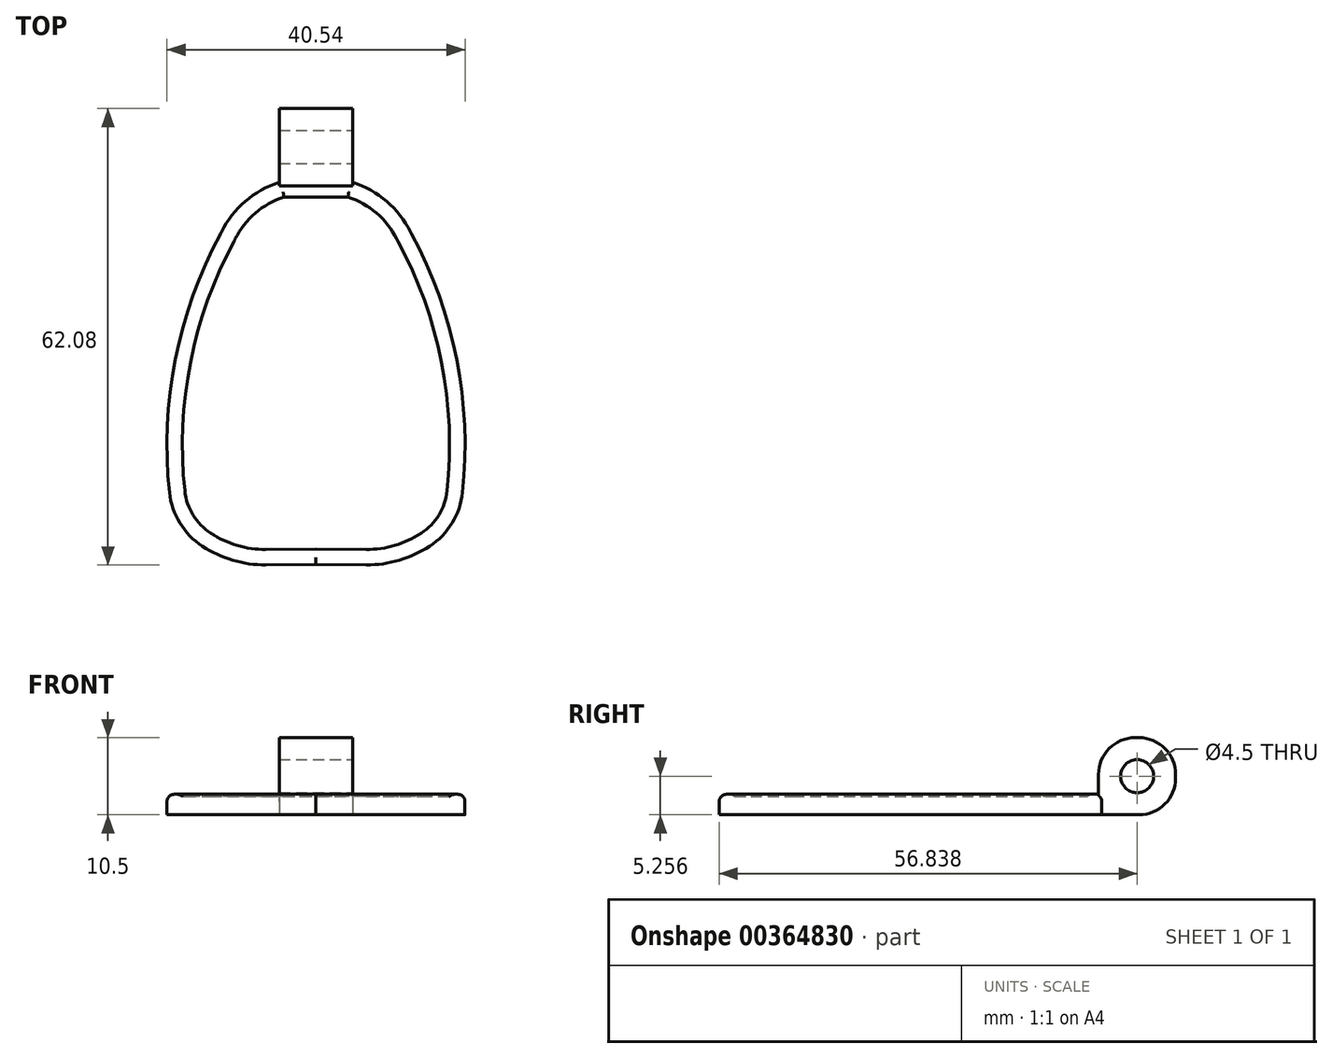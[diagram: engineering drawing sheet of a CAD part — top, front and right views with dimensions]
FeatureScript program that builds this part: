
annotation { "Feature Type Name" : "Feature", "Feature Type Description" : "" }
export const myFeature = defineFeature(function(context is Context, id is Id, definition is map)
    precondition{}
    {
        {
            var Q0;
            Q0=qCreatedBy(makeId("Top.planeOp"),FACE);
            var sketch = newSketch(context, id + "F0", { "sketchPlane" : qUnion([Q0])});
            skPoint(sketch, "E0.endSnap0", {"position": v(-0.73, -44.7) * mm});
            skArc(sketch, "E1", {"start": v(12.92, 6.57) * mm, "mid": v(8.04, 12.02) * mm, "end": v(1.01, 14.08) * mm});
            skArc(sketch, "E2", {"start": v(19.44, -32.3) * mm, "mid": v(19.43, -12.32) * mm, "end": v(12.92, 6.57) * mm});
            skArc(sketch, "E3.0", {"start": v(11.05, 5.6) * mm, "mid": v(6.94, 10.23) * mm, "end": v(1, 11.98) * mm});
            skArc(sketch, "E3.1", {"start": v(17.44, -31.52) * mm, "mid": v(17.32, -12.43) * mm, "end": v(11.05, 5.6) * mm});
            skArc(sketch, "E3.2", {"start": v(9.45, -35.83) * mm, "mid": v(13.96, -34.64) * mm, "end": v(17.44, -31.52) * mm});
            skArc(sketch, "E3.3", {"start": v(0, -36.35) * mm, "mid": v(4.75, -36.53) * mm, "end": v(9.45, -35.83) * mm});
            skPoint(sketch, "E4.orphan", {"position": v(0, 29.56) * mm});
            skPoint(sketch, "E0.end.orphan", {"position": v(-0.73, -55.53) * mm});
            skPoint(sketch, "E5.start.orphan", {"position": v(-6.8, -38.6) * mm});
            skPoint(sketch, "E6.visualSharp", {"position": v(-18.12, -32.94) * mm});
            skLineSegment(sketch, "E7", {"start": v(0, 11.88) * mm, "end": v(0, -48) * mm});
            skArc(sketch, "E8.MirrorCS", {"start": v(-11.05, 5.6) * mm, "mid": v(-6.94, 10.23) * mm, "end": v(-1, 11.98) * mm});
            skArc(sketch, "E9.MirrorCS", {"start": v(-17.44, -31.52) * mm, "mid": v(-17.32, -12.43) * mm, "end": v(-11.05, 5.6) * mm});
            skArc(sketch, "E10.MirrorCS", {"start": v(-9.45, -35.83) * mm, "mid": v(-13.96, -34.64) * mm, "end": v(-17.44, -31.52) * mm});
            skArc(sketch, "E11.MirrorCS", {"start": v(0, -36.35) * mm, "mid": v(-4.75, -36.53) * mm, "end": v(-9.45, -35.83) * mm});
            skArc(sketch, "E12.MirrorCS", {"start": v(-19.44, -32.3) * mm, "mid": v(-19.43, -12.32) * mm, "end": v(-12.92, 6.57) * mm});
            skArc(sketch, "E13.MirrorCS", {"start": v(-12.92, 6.57) * mm, "mid": v(-8.04, 12.02) * mm, "end": v(-1.01, 14.08) * mm});
            skLineSegment(sketch, "E14.bottom", {"start": v(5, 12.98) * mm, "end": v(-5, 12.98) * mm});
            skLineSegment(sketch, "E14.top", {"start": v(5, 23.48) * mm, "end": v(-5, 23.48) * mm});
            skLineSegment(sketch, "E14.left", {"start": v(5, 12.98) * mm, "end": v(5, 23.48) * mm});
            skLineSegment(sketch, "E14.right", {"start": v(-5, 12.98) * mm, "end": v(-5, 23.48) * mm});
            skPoint(sketch, "E14.middle", {"position": v(0, 18.23) * mm});
            skLineSegment(sketch, "E15", {"start": v(-1, 11.98) * mm, "end": v(1, 11.98) * mm});
            skPoint(sketch, "E16.MirrorCS.end.orphan", {"position": v(-9.73, -37.92) * mm});
            skPoint(sketch, "E17.MirrorCS.end.orphan", {"position": v(-19.44, -32.3) * mm});
            skPoint(sketch, "E18.orphan", {"position": v(-1.4, -38.6) * mm});
            skPoint(sketch, "E19.start.orphan", {"position": v(1.4, -38.6) * mm});
            skPoint(sketch, "E20.start.orphan", {"position": v(9.73, -37.92) * mm});
            skArc(sketch, "E21", {"start": v(-19.44, -32.3) * mm, "mid": v(-13.87, -36.96) * mm, "end": v(-6.8, -38.6) * mm});
            skLineSegment(sketch, "E22", {"start": v(-6.8, -38.6) * mm, "end": v(0, -38.56) * mm});
            skLineSegment(sketch, "E23.MirrorCS", {"start": v(6.8, -38.6) * mm, "end": v(0, -38.56) * mm});
            skArc(sketch, "E24.MirrorCS", {"start": v(19.44, -32.3) * mm, "mid": v(13.87, -36.96) * mm, "end": v(6.8, -38.6) * mm});
            skSolve(sketch);
        }
        {
            var Q0;
            {var subQ3=sQuery(id+"F0.wireOp",EDGE,"E14.bottom");Q0=makeQuery(id+"F0.imprint","IMPRINT",FACE,{"disambiguationData":[TD([[makeQuery(id+"F0.imprint","IMPRINT",EDGE,{"derivedFrom":subQ3}),-1.0]])]});}
            var Q1;
            Q1=makeQuery(id+"F0.imprint","IMPRINT",FACE,{"disambiguationData":[TD([[makeQuery(id+"F0.imprint","IMPRINT",EDGE,{"derivedFrom":sQuery(id+"F0.wireOp",EDGE,"E3.0")}),1.0]])]});
            var Q2;
            {var subQ0=sQuery(id+"F0.wireOp",EDGE,"E2");Q2=makeQuery(id+"F0.imprint","IMPRINT",FACE,{"disambiguationData":[TD([[makeQuery(id+"F0.imprint","IMPRINT",EDGE,{"derivedFrom":subQ0}),1.0]])]});}
            extrude(context, id + "F1", {"entities" : qUnion([Q0, Q1, Q2]), "depth" : 2.5 * mm});
        }
        {
            var Q0;
            {var subQ3=sQuery(id+"F0.wireOp",EDGE,"E14.bottom");Q0=makeQuery(id+"F0.imprint","IMPRINT",FACE,{"disambiguationData":[TD([[makeQuery(id+"F0.imprint","IMPRINT",EDGE,{"derivedFrom":subQ3}),-1.0]])]});}
            extrude(context, id + "F2", {"entities" : qUnion([Q0]), "operationType" : NewBodyOperationType.ADD, "depth" : 10.5 * mm});
        }
        {
            var Q0;
            Q0=makeQuery(id+"F2.opExtrude","CAP_EDGE",EDGE,{"disambiguationData":[OSD([sQuery(id+"F0.wireOp",EDGE,"E14.top")])],"isStart":false});
            var Q1;
            Q1=makeQuery(id+"F2.opExtrude","CAP_EDGE",EDGE,{"disambiguationData":[OSD([sQuery(id+"F0.wireOp",EDGE,"E14.bottom")])],"isStart":false});
            var Q2;
            Q2=makeQuery(id+"F1.opExtrude","CAP_EDGE",EDGE,{"disambiguationData":[OSD([sQuery(id+"F0.wireOp",EDGE,"E14.top")])],"isStart":true});
            fillet(context, id + "F3", {"entities" : qUnion([Q0, Q1, Q2]), "radius" : 5 * mm, "tangentPropagation" : true, "allowEdgeOverflow" : false});
        }
        {
            var Q0;
            Q0=makeQuery(id+"F1.opExtrude","SWEPT_EDGE",EDGE,{"disambiguationData":[OSD([sQuery(id+"F0.wireOp",EDGE,"E2"),sQuery(id+"F0.wireOp",EDGE,"E20")])]});
            var Q1;
            Q1=makeQuery(id+"F1.opExtrude","SWEPT_EDGE",EDGE,{"disambiguationData":[OSD([sQuery(id+"F0.wireOp",EDGE,"E1"),sQuery(id+"F0.wireOp",EDGE,"E2")])]});
            var Q2;
            Q2=makeQuery(id+"F1.opExtrude","SWEPT_EDGE",EDGE,{"disambiguationData":[OSD([sQuery(id+"F0.wireOp",EDGE,"E12.MirrorCS"),sQuery(id+"F0.wireOp",EDGE,"E13.MirrorCS")])]});
            var Q3;
            Q3=makeQuery(id+"F1.opExtrude","SWEPT_EDGE",EDGE,{"disambiguationData":[OSD([sQuery(id+"F0.wireOp",EDGE,"E17.MirrorCS"),sQuery(id+"F0.wireOp",EDGE,"E12.MirrorCS")])]});
            fillet(context, id + "F4", {"entities" : qUnion([Q0, Q1, Q2, Q3]), "radius" : 10 * mm, "tangentPropagation" : true, "allowEdgeOverflow" : false});
        }
        {
            var Q0;
            Q0=makeQuery(id+"F1.opExtrude","CAP_FACE",FACE,{"disambiguationData":[OSD([sQuery(id+"F0.wireOp",EDGE,"E1"),sQuery(id+"F0.wireOp",EDGE,"E2"),sQuery(id+"F0.wireOp",EDGE,"E12.MirrorCS"),sQuery(id+"F0.wireOp",EDGE,"E13.MirrorCS"),sQuery(id+"F0.wireOp",EDGE,"E14.top"),sQuery(id+"F0.wireOp",EDGE,"E14.left"),sQuery(id+"F0.wireOp",EDGE,"E14.right"),sQuery(id+"F0.wireOp",EDGE,"E21"),sQuery(id+"F0.wireOp",EDGE,"E22"),sQuery(id+"F0.wireOp",EDGE,"E23.MirrorCS"),sQuery(id+"F0.wireOp",EDGE,"E24.MirrorCS")])],"isStart":false});
            var sketch = newSketch(context, id + "F5", { "sketchPlane" : qUnion([Q0])});
            skArc(sketch, "E25.0", {"start": v(10.98, 5.76) * mm, "mid": v(8.24, 9.27) * mm, "end": v(4.36, 11.44) * mm});
            skArc(sketch, "E25.1", {"start": v(11.16, 5.41) * mm, "mid": v(11.06, 5.58) * mm, "end": v(10.98, 5.76) * mm});
            skArc(sketch, "E25.2", {"start": v(-17.84, -28.52) * mm, "mid": v(-16.72, -31.8) * mm, "end": v(-14.3, -34.29) * mm});
            skArc(sketch, "E25.3", {"start": v(-17.84, -28.52) * mm, "mid": v(-17.07, -11.05) * mm, "end": v(-11.16, 5.41) * mm});
            skArc(sketch, "E25.4", {"start": v(-10.98, 5.76) * mm, "mid": v(-11.06, 5.58) * mm, "end": v(-11.16, 5.41) * mm});
            skArc(sketch, "E25.5", {"start": v(-10.98, 5.76) * mm, "mid": v(-8.24, 9.27) * mm, "end": v(-4.36, 11.44) * mm});
            skArc(sketch, "E25.6", {"start": v(-14.3, -34.29) * mm, "mid": v(-10.72, -35.95) * mm, "end": v(-6.82, -36.5) * mm});
            skLineSegment(sketch, "E25.7", {"start": v(-6.82, -36.5) * mm, "end": v(0, -36.46) * mm});
            skLineSegment(sketch, "E25.8", {"start": v(6.82, -36.5) * mm, "end": v(0, -36.46) * mm});
            skArc(sketch, "E25.9", {"start": v(14.3, -34.29) * mm, "mid": v(10.72, -35.95) * mm, "end": v(6.82, -36.5) * mm});
            skArc(sketch, "E25.10", {"start": v(14.3, -34.29) * mm, "mid": v(16.72, -31.8) * mm, "end": v(17.84, -28.52) * mm});
            skArc(sketch, "E25.11", {"start": v(17.84, -28.52) * mm, "mid": v(17.07, -11.05) * mm, "end": v(11.16, 5.41) * mm});
            skLineSegment(sketch, "E26", {"start": v(-4.36, 11.44) * mm, "end": v(4.36, 11.44) * mm});
            skSolve(sketch);
        }
        {
            var Q0;
            Q0=makeQuery(id+"F5.imprint","IMPRINT",FACE,{"disambiguationData":[TD([[makeQuery(id+"F5.imprint","IMPRINT",EDGE,{"derivedFrom":sQuery(id+"F5.wireOp",EDGE,"E25.0")}),-1.0]])]});
            extrude(context, id + "F6", {"entities" : qUnion([Q0]), "operationType" : NewBodyOperationType.ADD, "depth" : 0.3 * mm});
        }
        {
            var Q0;
            Q0=makeQuery(id+"F6.opExtrude","CAP_EDGE",EDGE,{"disambiguationData":[OSD([sQuery(id+"F5.wireOp",EDGE,"E25.0")])],"isStart":false});
            var Q1;
            Q1=makeQuery(id+"F6.opExtrude","CAP_EDGE",EDGE,{"disambiguationData":[OSD([sQuery(id+"F5.wireOp",EDGE,"E26")])],"isStart":false});
            var Q2;
            Q2=makeQuery(id+"F6.opExtrude","CAP_EDGE",EDGE,{"disambiguationData":[OSD([sQuery(id+"F5.wireOp",EDGE,"E25.5")])],"isStart":false});
            var Q3;
            Q3=makeQuery(id+"F6.opExtrude","CAP_EDGE",EDGE,{"disambiguationData":[OSD([sQuery(id+"F5.wireOp",EDGE,"E25.3")])],"isStart":false});
            var Q4;
            Q4=makeQuery(id+"F6.opExtrude","CAP_EDGE",EDGE,{"disambiguationData":[OSD([sQuery(id+"F5.wireOp",EDGE,"E25.2")])],"isStart":false});
            var Q5;
            Q5=makeQuery(id+"F6.opExtrude","CAP_EDGE",EDGE,{"disambiguationData":[OSD([sQuery(id+"F5.wireOp",EDGE,"E25.11")])],"isStart":false});
            var Q6;
            Q6=makeQuery(id+"F6.opExtrude","CAP_EDGE",EDGE,{"disambiguationData":[OSD([sQuery(id+"F5.wireOp",EDGE,"E25.10")])],"isStart":false});
            var Q7;
            Q7=makeQuery(id+"F6.opExtrude","CAP_EDGE",EDGE,{"disambiguationData":[OSD([sQuery(id+"F5.wireOp",EDGE,"E25.7")])],"isStart":false});
            var Q8;
            Q8=makeQuery(id+"F6.opExtrude","CAP_EDGE",EDGE,{"disambiguationData":[OSD([sQuery(id+"F5.wireOp",EDGE,"E25.8")])],"isStart":false});
            var Q9;
            Q9=makeQuery(id+"F6.opExtrude","CAP_EDGE",EDGE,{"disambiguationData":[OSD([sQuery(id+"F5.wireOp",EDGE,"E25.9")])],"isStart":false});
            var Q10;
            Q10=makeQuery(id+"F6.opExtrude","CAP_EDGE",EDGE,{"disambiguationData":[OSD([sQuery(id+"F5.wireOp",EDGE,"E25.6")])],"isStart":false});
            var Q11;
            Q11=makeQuery(id+"F6.opExtrude","CAP_EDGE",EDGE,{"disambiguationData":[OSD([sQuery(id+"F5.wireOp",EDGE,"E25.1")])],"isStart":false});
            var Q12;
            Q12=makeQuery(id+"F6.opExtrude","CAP_EDGE",EDGE,{"disambiguationData":[OSD([sQuery(id+"F5.wireOp",EDGE,"E25.4")])],"isStart":false});
            fillet(context, id + "F7", {"entities" : qUnion([Q0, Q1, Q2, Q3, Q4, Q5, Q6, Q7, Q8, Q9, Q10, Q11, Q12]), "radius" : 1 * mm, "tangentPropagation" : true, "allowEdgeOverflow" : false});
        }
        {
            var Q0;
            Q0=makeQuery(id+"F6.opExtrude","CAP_EDGE",EDGE,{"disambiguationData":[OSD([sQuery(id+"F0.wireOp",EDGE,"E1")])],"isStart":false});
            var Q1;
            Q1=makeQuery(id+"F6.opExtrude","CAP_EDGE",EDGE,{"disambiguationData":[OSD([sQuery(id+"F0.wireOp",EDGE,"E2")])],"isStart":false});
            var Q2;
            {var subQ0=sQuery(id+"F0.wireOp",EDGE,"E24.MirrorCS");var subQ1=sQuery(id+"F0.wireOp",EDGE,"E23.MirrorCS");var subQ2=sQuery(id+"F0.wireOp",EDGE,"E22");var subQ3=sQuery(id+"F0.wireOp",EDGE,"E21");var subQ4=sQuery(id+"F0.wireOp",EDGE,"E14.right");var subQ5=sQuery(id+"F0.wireOp",EDGE,"E14.left");var subQ6=sQuery(id+"F0.wireOp",EDGE,"E14.top");var subQ7=sQuery(id+"F0.wireOp",EDGE,"E13.MirrorCS");var subQ8=sQuery(id+"F0.wireOp",EDGE,"E12.MirrorCS");var subQ9=sQuery(id+"F0.wireOp",EDGE,"E2");var subQ10=sQuery(id+"F0.wireOp",EDGE,"E1");Q2=makeQuery(id+"F6.opExtrude","CAP_EDGE",EDGE,{"disambiguationData":[OSD([subQ10,subQ9,subQ8,subQ7,subQ6,subQ5,subQ4,subQ3,subQ2,subQ1,subQ0]),TDD([makeQuery(id+"F5.imprint","IMPRINT",EDGE,{"derivedFrom":makeQuery(id+"F4.opFillet","BLEND_EDGE",EDGE,{"blendedFrom":[makeQuery(id+"F1.opExtrude","SWEPT_EDGE",EDGE,{"disambiguationData":[OSD([subQ9,subQ0])]}),makeQuery(id+"F1.opExtrude","CAP_FACE",FACE,{"disambiguationData":[OSD([subQ10,subQ9,subQ8,subQ7,subQ6,subQ5,subQ4,subQ3,subQ2,subQ1,subQ0])],"isStart":false})],"blendedInto":[makeQuery(id+"F1.opExtrude","CAP_FACE",FACE,{"disambiguationData":[OSD([subQ10,subQ9,subQ8,subQ7,subQ6,subQ5,subQ4,subQ3,subQ2,subQ1,subQ0])],"isStart":false})]})})])],"isStart":false});}
            var Q3;
            Q3=makeQuery(id+"F6.opExtrude","CAP_EDGE",EDGE,{"disambiguationData":[OSD([sQuery(id+"F0.wireOp",EDGE,"E24.MirrorCS")])],"isStart":false});
            var Q4;
            Q4=makeQuery(id+"F6.opExtrude","CAP_EDGE",EDGE,{"disambiguationData":[OSD([sQuery(id+"F0.wireOp",EDGE,"E23.MirrorCS")])],"isStart":false});
            var Q5;
            Q5=makeQuery(id+"F6.opExtrude","CAP_EDGE",EDGE,{"disambiguationData":[OSD([sQuery(id+"F0.wireOp",EDGE,"E22")])],"isStart":false});
            var Q6;
            Q6=makeQuery(id+"F6.opExtrude","CAP_EDGE",EDGE,{"disambiguationData":[OSD([sQuery(id+"F0.wireOp",EDGE,"E21")])],"isStart":false});
            var Q7;
            {var subQ0=sQuery(id+"F0.wireOp",EDGE,"E24.MirrorCS");var subQ1=sQuery(id+"F0.wireOp",EDGE,"E23.MirrorCS");var subQ2=sQuery(id+"F0.wireOp",EDGE,"E22");var subQ3=sQuery(id+"F0.wireOp",EDGE,"E21");var subQ4=sQuery(id+"F0.wireOp",EDGE,"E14.right");var subQ5=sQuery(id+"F0.wireOp",EDGE,"E14.left");var subQ6=sQuery(id+"F0.wireOp",EDGE,"E14.top");var subQ7=sQuery(id+"F0.wireOp",EDGE,"E13.MirrorCS");var subQ8=sQuery(id+"F0.wireOp",EDGE,"E12.MirrorCS");var subQ9=sQuery(id+"F0.wireOp",EDGE,"E2");var subQ10=sQuery(id+"F0.wireOp",EDGE,"E1");Q7=makeQuery(id+"F6.opExtrude","CAP_EDGE",EDGE,{"disambiguationData":[OSD([subQ10,subQ9,subQ8,subQ7,subQ6,subQ5,subQ4,subQ3,subQ2,subQ1,subQ0]),TDD([makeQuery(id+"F5.imprint","IMPRINT",EDGE,{"derivedFrom":makeQuery(id+"F4.opFillet","BLEND_EDGE",EDGE,{"blendedFrom":[makeQuery(id+"F1.opExtrude","SWEPT_EDGE",EDGE,{"disambiguationData":[OSD([subQ8,subQ3])]}),makeQuery(id+"F1.opExtrude","CAP_FACE",FACE,{"disambiguationData":[OSD([subQ10,subQ9,subQ8,subQ7,subQ6,subQ5,subQ4,subQ3,subQ2,subQ1,subQ0])],"isStart":false})],"blendedInto":[makeQuery(id+"F1.opExtrude","CAP_FACE",FACE,{"disambiguationData":[OSD([subQ10,subQ9,subQ8,subQ7,subQ6,subQ5,subQ4,subQ3,subQ2,subQ1,subQ0])],"isStart":false})]})})])],"isStart":false});}
            var Q8;
            Q8=makeQuery(id+"F6.opExtrude","CAP_EDGE",EDGE,{"disambiguationData":[OSD([sQuery(id+"F0.wireOp",EDGE,"E12.MirrorCS")])],"isStart":false});
            var Q9;
            Q9=makeQuery(id+"F6.opExtrude","CAP_EDGE",EDGE,{"disambiguationData":[OSD([sQuery(id+"F0.wireOp",EDGE,"E13.MirrorCS")])],"isStart":false});
            var Q10;
            {var subQ0=sQuery(id+"F0.wireOp",EDGE,"E24.MirrorCS");var subQ1=sQuery(id+"F0.wireOp",EDGE,"E23.MirrorCS");var subQ2=sQuery(id+"F0.wireOp",EDGE,"E22");var subQ3=sQuery(id+"F0.wireOp",EDGE,"E21");var subQ4=sQuery(id+"F0.wireOp",EDGE,"E14.right");var subQ5=sQuery(id+"F0.wireOp",EDGE,"E14.left");var subQ6=sQuery(id+"F0.wireOp",EDGE,"E14.top");var subQ7=sQuery(id+"F0.wireOp",EDGE,"E13.MirrorCS");var subQ8=sQuery(id+"F0.wireOp",EDGE,"E12.MirrorCS");var subQ9=sQuery(id+"F0.wireOp",EDGE,"E2");var subQ10=sQuery(id+"F0.wireOp",EDGE,"E1");Q10=makeQuery(id+"F6.opExtrude","CAP_EDGE",EDGE,{"disambiguationData":[OSD([subQ10,subQ9,subQ8,subQ7,subQ6,subQ5,subQ4,subQ3,subQ2,subQ1,subQ0]),TDD([makeQuery(id+"F5.imprint","IMPRINT",EDGE,{"derivedFrom":makeQuery(id+"F4.opFillet","BLEND_EDGE",EDGE,{"blendedFrom":[makeQuery(id+"F1.opExtrude","SWEPT_EDGE",EDGE,{"disambiguationData":[OSD([subQ10,subQ9])]}),makeQuery(id+"F1.opExtrude","CAP_FACE",FACE,{"disambiguationData":[OSD([subQ10,subQ9,subQ8,subQ7,subQ6,subQ5,subQ4,subQ3,subQ2,subQ1,subQ0])],"isStart":false})],"blendedInto":[makeQuery(id+"F1.opExtrude","CAP_FACE",FACE,{"disambiguationData":[OSD([subQ10,subQ9,subQ8,subQ7,subQ6,subQ5,subQ4,subQ3,subQ2,subQ1,subQ0])],"isStart":false})]})})])],"isStart":false});}
            var Q11;
            {var subQ0=sQuery(id+"F0.wireOp",EDGE,"E24.MirrorCS");var subQ1=sQuery(id+"F0.wireOp",EDGE,"E23.MirrorCS");var subQ2=sQuery(id+"F0.wireOp",EDGE,"E22");var subQ3=sQuery(id+"F0.wireOp",EDGE,"E21");var subQ4=sQuery(id+"F0.wireOp",EDGE,"E14.right");var subQ5=sQuery(id+"F0.wireOp",EDGE,"E14.left");var subQ6=sQuery(id+"F0.wireOp",EDGE,"E14.top");var subQ7=sQuery(id+"F0.wireOp",EDGE,"E13.MirrorCS");var subQ8=sQuery(id+"F0.wireOp",EDGE,"E12.MirrorCS");var subQ9=sQuery(id+"F0.wireOp",EDGE,"E2");var subQ10=sQuery(id+"F0.wireOp",EDGE,"E1");Q11=makeQuery(id+"F6.opExtrude","CAP_EDGE",EDGE,{"disambiguationData":[OSD([subQ10,subQ9,subQ8,subQ7,subQ6,subQ5,subQ4,subQ3,subQ2,subQ1,subQ0]),TDD([makeQuery(id+"F5.imprint","IMPRINT",EDGE,{"derivedFrom":makeQuery(id+"F4.opFillet","BLEND_EDGE",EDGE,{"blendedFrom":[makeQuery(id+"F1.opExtrude","SWEPT_EDGE",EDGE,{"disambiguationData":[OSD([subQ8,subQ7])]}),makeQuery(id+"F1.opExtrude","CAP_FACE",FACE,{"disambiguationData":[OSD([subQ10,subQ9,subQ8,subQ7,subQ6,subQ5,subQ4,subQ3,subQ2,subQ1,subQ0])],"isStart":false})],"blendedInto":[makeQuery(id+"F1.opExtrude","CAP_FACE",FACE,{"disambiguationData":[OSD([subQ10,subQ9,subQ8,subQ7,subQ6,subQ5,subQ4,subQ3,subQ2,subQ1,subQ0])],"isStart":false})]})})])],"isStart":false});}
            fillet(context, id + "F8", {"entities" : qUnion([Q0, Q1, Q2, Q3, Q4, Q5, Q6, Q7, Q8, Q9, Q10, Q11]), "radius" : 1 * mm, "tangentPropagation" : true, "allowEdgeOverflow" : false});
        }
        {
            var Q0;
            {var subQ0=sQuery(id+"F0.wireOp",EDGE,"E14.left");Q0=makeQuery(id+"F2.boolean.opBoolean","MERGE",FACE,{"derivedFrom":[makeQuery(id+"F1.opExtrude","SWEPT_FACE",FACE,{"disambiguationData":[OSD([subQ0])]}),makeQuery(id+"F2.opExtrude","SWEPT_FACE",FACE,{"disambiguationData":[OSD([subQ0])]})]});}
            var sketch = newSketch(context, id + "F9", { "sketchPlane" : qUnion([Q0])});
            skCircle(sketch, "E27", {"center": v(18.24, 5.26) * mm, "radius": 2.25 * mm});
            skSolve(sketch);
        }
        {
            var Q0;
            Q0=makeQuery(id+"F9.imprint","IMPRINT",FACE,{"disambiguationData":[TD([[makeQuery(id+"F9.imprint","IMPRINT",EDGE,{"derivedFrom":sQuery(id+"F9.wireOp",EDGE,"E27")}),1.0]])]});
            extrude(context, id + "F10", {"entities" : qUnion([Q0]), "operationType" : NewBodyOperationType.REMOVE, "oppositeDirection" : true, "depth" : 25 * mm});
        }
    });
